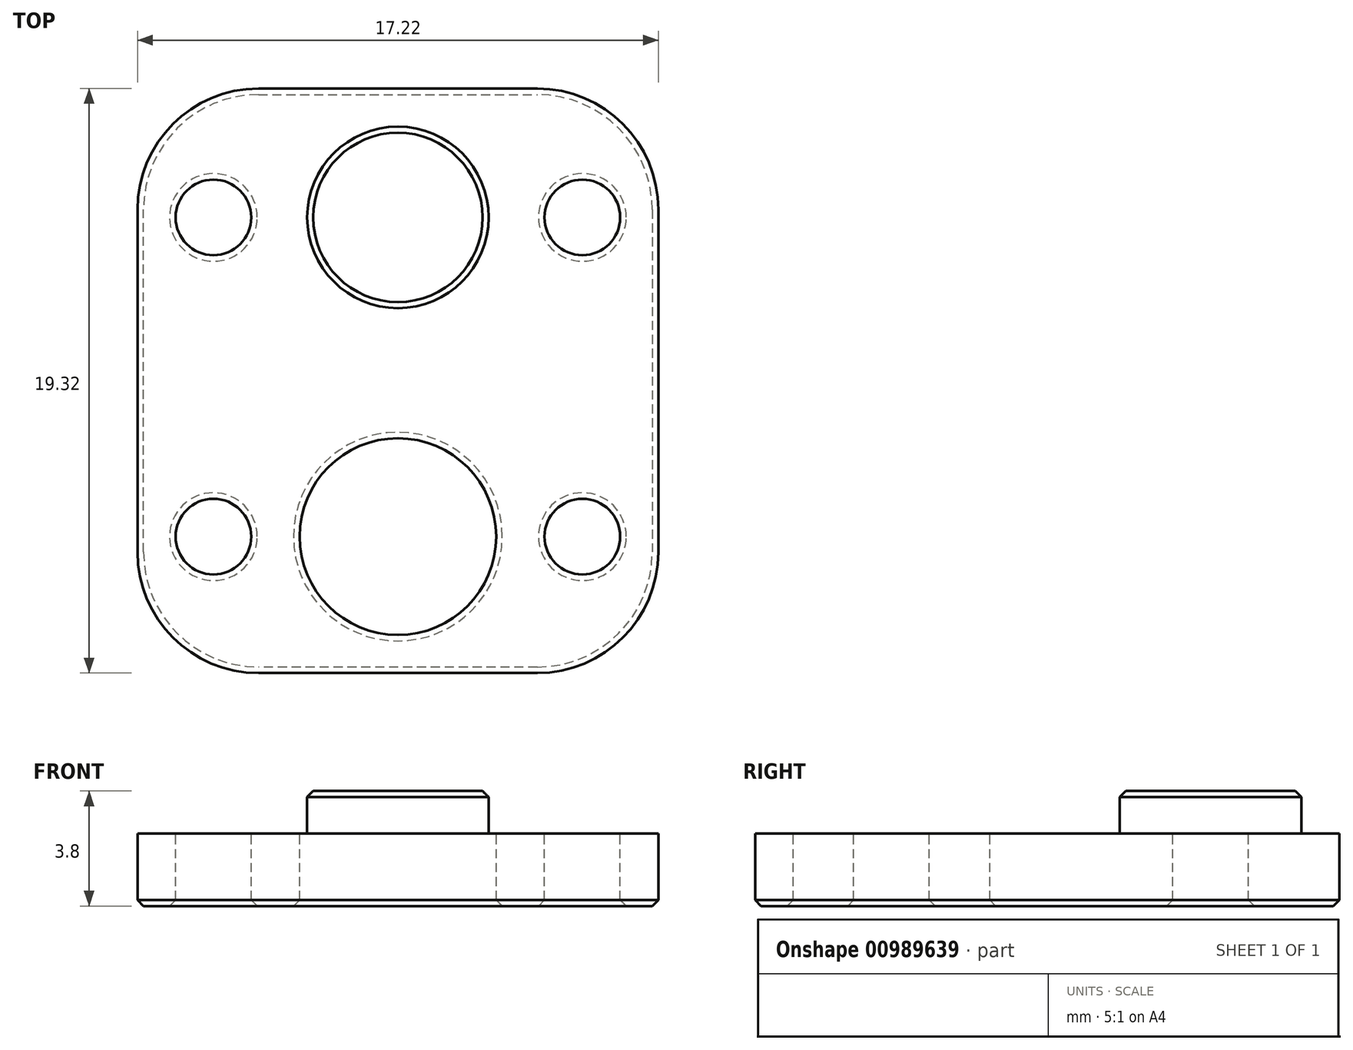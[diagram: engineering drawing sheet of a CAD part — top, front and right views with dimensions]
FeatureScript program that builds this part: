
annotation { "Feature Type Name" : "Feature", "Feature Type Description" : "" }
export const myFeature = defineFeature(function(context is Context, id is Id, definition is map)
    precondition{}
    {
        {
            var Q0;
            Q0=qCreatedBy(makeId("Top.planeOp"),FACE);
            var sketch = newSketch(context, id + "F0", { "sketchPlane" : qUnion([Q0])});
            skCircle(sketch, "E0", {"center": v(0, 0) * mm, "radius": 3 * mm});
            skCircle(sketch, "E1", {"center": v(-6.1, 0) * mm, "radius": 1.25 * mm});
            skLineSegment(sketch, "E2", {"start": v(0, 0) * mm, "end": v(0, 11.94) * mm, "construction": true});
            skCircle(sketch, "E3.MirrorC", {"center": v(6.1, 0) * mm, "radius": 1.25 * mm});
            skLineSegment(sketch, "E4.bottom", {"start": v(4.6, 4.26) * mm, "end": v(-4.6, 4.26) * mm});
            skLineSegment(sketch, "E4.top", {"start": v(8.6, -4.26) * mm, "end": v(-8.6, -4.26) * mm});
            skLineSegment(sketch, "E4.left", {"start": v(8.6, 0.26) * mm, "end": v(8.6, -4.26) * mm});
            skLineSegment(sketch, "E4.right", {"start": v(-8.6, 0.26) * mm, "end": v(-8.6, -4.26) * mm});
            skPoint(sketch, "E5.visualSharp", {"position": v(-8.6, 4.26) * mm});
            skArc(sketch, "E5.filletArc", {"start": v(-4.6, 4.26) * mm, "mid": v(-7.44, 3.09) * mm, "end": v(-8.6, 0.26) * mm});
            skPoint(sketch, "E6.visualSharp", {"position": v(8.6, 4.26) * mm});
            skArc(sketch, "E6.filletArc", {"start": v(8.6, 0.26) * mm, "mid": v(7.44, 3.09) * mm, "end": v(4.6, 4.26) * mm});
            skLineSegment(sketch, "E7.bottom", {"start": v(-8.6, -4.26) * mm, "end": v(8.6, -4.26) * mm});
            skLineSegment(sketch, "E7.top", {"start": v(-4.61, -15.06) * mm, "end": v(4.6, -15.06) * mm});
            skLineSegment(sketch, "E7.left", {"start": v(-8.61, -4.26) * mm, "end": v(-8.61, -11.06) * mm});
            skLineSegment(sketch, "E7.right", {"start": v(8.6, -4.26) * mm, "end": v(8.6, -11.06) * mm});
            skCircle(sketch, "E8", {"center": v(0, -10.55) * mm, "radius": 3.25 * mm});
            skCircle(sketch, "E9", {"center": v(-6.1, -10.55) * mm, "radius": 1.25 * mm});
            skCircle(sketch, "E10.MirrorC", {"center": v(6.1, -10.55) * mm, "radius": 1.25 * mm});
            skPoint(sketch, "E11.visualSharp", {"position": v(-8.61, -15.06) * mm});
            skArc(sketch, "E11.filletArc", {"start": v(-8.61, -11.06) * mm, "mid": v(-7.44, -13.89) * mm, "end": v(-4.61, -15.06) * mm});
            skPoint(sketch, "E12.visualSharp", {"position": v(8.6, -15.06) * mm});
            skArc(sketch, "E12.filletArc", {"start": v(4.6, -15.06) * mm, "mid": v(7.44, -13.89) * mm, "end": v(8.6, -11.06) * mm});
            skCircle(sketch, "E13", {"center": v(0, -10.55) * mm, "radius": 3.85 * mm, "construction": true});
            skSolve(sketch);
        }
        {
            var Q0;
            Q0=makeQuery(id+"F0.imprint","IMPRINT",FACE,{"disambiguationData":[TD([[makeQuery(id+"F0.imprint","IMPRINT",EDGE,{"derivedFrom":sQuery(id+"F0.wireOp",EDGE,"E0")}),-1.0]])]});
            var Q1;
            Q1=makeQuery(id+"F0.imprint","IMPRINT",FACE,{"disambiguationData":[TD([[makeQuery(id+"F0.imprint","IMPRINT",EDGE,{"derivedFrom":sQuery(id+"F0.wireOp",EDGE,"E7.bottom")}),-1.0]])]});
            var Q2;
            Q2=makeQuery(id+"F0.imprint","IMPRINT",FACE,{"disambiguationData":[TD([[makeQuery(id+"F0.imprint","IMPRINT",EDGE,{"derivedFrom":sQuery(id+"F0.wireOp",EDGE,"E0")}),1.0]])]});
            var Q3;
            Q3=makeQuery(id+"F0.imprint","IMPRINT",FACE,{"disambiguationData":[TD([[makeQuery(id+"F0.imprint","IMPRINT",EDGE,{"derivedFrom":sQuery(id+"F0.wireOp",EDGE,"E8")}),-1.0]])]});
            extrude(context, id + "F1", {"entities" : qUnion([Q0, Q1, Q2, Q3]), "oppositeDirection" : true, "depth" : (1.4 + 1) * mm, "offsetDistance" : 25 * mm});
        }
        {
            var Q0;
            Q0=makeQuery(id+"F0.imprint","IMPRINT",FACE,{"disambiguationData":[TD([[makeQuery(id+"F0.imprint","IMPRINT",EDGE,{"derivedFrom":sQuery(id+"F0.wireOp",EDGE,"E0")}),1.0]])]});
            extrude(context, id + "F2", {"entities" : qUnion([Q0]), "operationType" : NewBodyOperationType.ADD, "depth" : 1.4 * mm, "offsetDistance" : 25 * mm});
        }
        {
            var Q0;
            Q0=makeQuery(id+"F1.opExtrude","CAP_FACE",FACE,{"disambiguationData":[OSD([sQuery(id+"F0.wireOp",EDGE,"E1"),sQuery(id+"F0.wireOp",EDGE,"E3.MirrorC"),sQuery(id+"F0.wireOp",EDGE,"E4.bottom"),sQuery(id+"F0.wireOp",EDGE,"E4.left"),sQuery(id+"F0.wireOp",EDGE,"E4.right"),sQuery(id+"F0.wireOp",EDGE,"E5.filletArc"),sQuery(id+"F0.wireOp",EDGE,"E6.filletArc"),sQuery(id+"F0.wireOp",EDGE,"E7.top"),sQuery(id+"F0.wireOp",EDGE,"E7.left"),sQuery(id+"F0.wireOp",EDGE,"E7.right"),sQuery(id+"F0.wireOp",EDGE,"E8"),sQuery(id+"F0.wireOp",EDGE,"E9"),sQuery(id+"F0.wireOp",EDGE,"E10.MirrorC"),sQuery(id+"F0.wireOp",EDGE,"E11.filletArc"),sQuery(id+"F0.wireOp",EDGE,"E12.filletArc")])],"isStart":false});
            chamfer(context, id + "F3", {"entities" : qUnion([Q0]), "width" : 0.2 * mm, "tangentPropagation" : true});
        }
        {
            var Q0;
            Q0=makeQuery(id+"F2.opExtrude","CAP_FACE",FACE,{"disambiguationData":[OSD([sQuery(id+"F0.wireOp",EDGE,"E0")])],"isStart":false});
            chamfer(context, id + "F4", {"entities" : qUnion([Q0]), "width" : 0.2 * mm, "tangentPropagation" : true});
        }
    });
